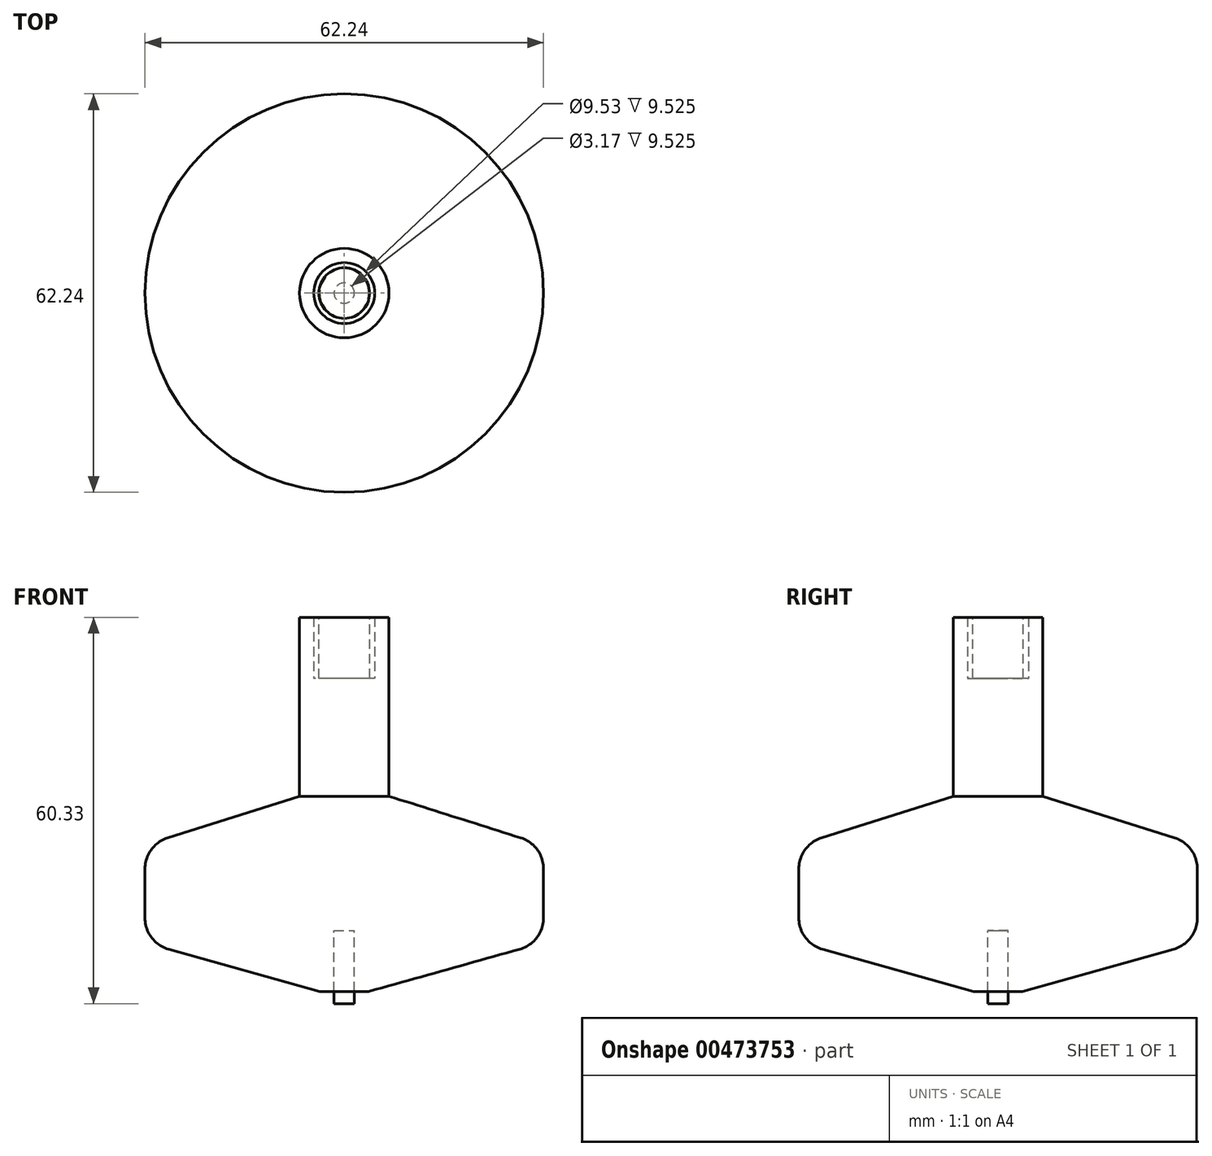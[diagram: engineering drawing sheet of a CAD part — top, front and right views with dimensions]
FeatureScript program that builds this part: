
annotation { "Feature Type Name" : "Feature", "Feature Type Description" : "" }
export const myFeature = defineFeature(function(context is Context, id is Id, definition is map)
    precondition{}
    {
        {
            var Q0;
            Q0=qCreatedBy(makeId("Front.planeOp"),FACE);
            var sketch = newSketch(context, id + "F0", { "sketchPlane" : qUnion([Q0])});
            skLineSegment(sketch, "E0", {"start": v(31.12, 12.07) * mm, "end": v(31.12, 27.3) * mm});
            skLineSegment(sketch, "E1", {"start": v(6.99, 62.87) * mm, "end": v(0, 62.87) * mm});
            skLineSegment(sketch, "E2", {"start": v(0, 62.87) * mm, "end": v(0, 4.45) * mm});
            skLineSegment(sketch, "E3", {"start": v(0, 4.45) * mm, "end": v(3.81, 4.45) * mm});
            skLineSegment(sketch, "E4", {"start": v(3.81, 4.45) * mm, "end": v(31.12, 12.07) * mm});
            skLineSegment(sketch, "E5", {"start": v(31.12, 27.3) * mm, "end": v(6.99, 34.93) * mm});
            skLineSegment(sketch, "E6", {"start": v(6.98, 34.93) * mm, "end": v(6.98, 62.87) * mm});
            skPoint(sketch, "E7", {"position": v(31.12, 19.69) * mm});
            skSolve(sketch);
        }
        {
            var Q0;
            Q0=makeQuery(id+"F0.imprint","IMPRINT",FACE,{"disambiguationData":[TD([[makeQuery(id+"F0.imprint","IMPRINT",EDGE,{"derivedFrom":sQuery(id+"F0.wireOp",EDGE,"E0")}),1.0]])]});
            var Q1;
            Q1=sQuery(id+"F0.wireOp",EDGE,"E2");
            revolve(context, id + "F1", {"entities" : qUnion([Q0]), "axis" : qUnion([Q1]), "revolveType" : RevolveType.FULL});
        }
        {
            var Q0;
            Q0=makeQuery(id+"F1.opRevolve","SWEPT_FACE",FACE,{"disambiguationData":[OSD([sQuery(id+"F0.wireOp",EDGE,"E1")])]});
            var sketch = newSketch(context, id + "F2", { "sketchPlane" : qUnion([Q0])});
            skCircle(sketch, "E8", {"center": v(0, 0) * mm, "radius": 4.76 * mm});
            skSolve(sketch);
        }
        {
            var Q0;
            Q0=makeQuery(id+"F2.imprint","IMPRINT",FACE,{"disambiguationData":[TD([[makeQuery(id+"F2.imprint","IMPRINT",EDGE,{"derivedFrom":sQuery(id+"F2.wireOp",EDGE,"E8")}),1.0]])]});
            extrude(context, id + "F3", {"entities" : qUnion([Q0]), "operationType" : NewBodyOperationType.REMOVE, "oppositeDirection" : true, "depth" : 9.52 * mm});
        }
        {
            var Q0;
            Q0=makeQuery(id+"F1.opRevolve","SWEPT_FACE",FACE,{"disambiguationData":[OSD([sQuery(id+"F0.wireOp",EDGE,"E3")])]});
            var sketch = newSketch(context, id + "F4", { "sketchPlane" : qUnion([Q0])});
            skCircle(sketch, "E9", {"center": v(0, 0) * mm, "radius": 1.59 * mm});
            skSolve(sketch);
        }
        {
            var Q0;
            Q0=qSketchRegion(id+"F4",true);
            extrude(context, id + "F5", {"entities" : qUnion([Q0]), "operationType" : NewBodyOperationType.REMOVE, "oppositeDirection" : true, "depth" : 9.52 * mm});
        }
        {
            var Q0;
            Q0=makeQuery(id+"F3.boolean.opBoolean","COPY",FACE,{"derivedFrom":makeQuery(id+"F3.opExtrude","CAP_FACE",FACE,{"disambiguationData":[OSD([sQuery(id+"F2.wireOp",EDGE,"E8")])],"isStart":false})});
            extrude(context, id + "F6", {"entities" : qUnion([Q0]), "depth" : 9.52 * mm});
        }
        {
            var Q0;
            Q0=makeQuery(id+"F6.opExtrude","CAP_FACE",FACE,{"disambiguationData":[OSD([sQuery(id+"F2.wireOp",EDGE,"E8")])],"isStart":false});
            var sketch = newSketch(context, id + "F7", { "sketchPlane" : qUnion([Q0])});
            skCircle(sketch, "E10", {"center": v(0, 0) * mm, "radius": 3.95 * mm});
            skSolve(sketch);
        }
        {
            var Q0;
            Q0=makeQuery(id+"F7.imprint","IMPRINT",FACE,{"disambiguationData":[TD([[makeQuery(id+"F7.imprint","IMPRINT",EDGE,{"derivedFrom":sQuery(id+"F7.wireOp",EDGE,"E10")}),1.0]])]});
            extrude(context, id + "F8", {"entities" : qUnion([Q0]), "operationType" : NewBodyOperationType.REMOVE, "oppositeDirection" : true, "depth" : 9.52 * mm});
        }
        {
            var Q0;
            Q0=makeQuery(id+"F5.boolean.opBoolean","COPY",FACE,{"derivedFrom":makeQuery(id+"F5.opExtrude","CAP_FACE",FACE,{"disambiguationData":[OSD([sQuery(id+"F4.wireOp",EDGE,"E9")])],"isStart":false})});
            extrude(context, id + "F9", {"entities" : qUnion([Q0]), "depth" : 11.43 * mm});
        }
        {
            var Q0;
            Q0=makeQuery(id+"F1.opRevolve","SWEPT_FACE",FACE,{"disambiguationData":[OSD([sQuery(id+"F0.wireOp",EDGE,"E0")])]});
            fillet(context, id + "F10", {"entities" : qUnion([Q0]), "radius" : 5.08 * mm, "tangentPropagation" : true, "allowEdgeOverflow" : false});
        }
    });
